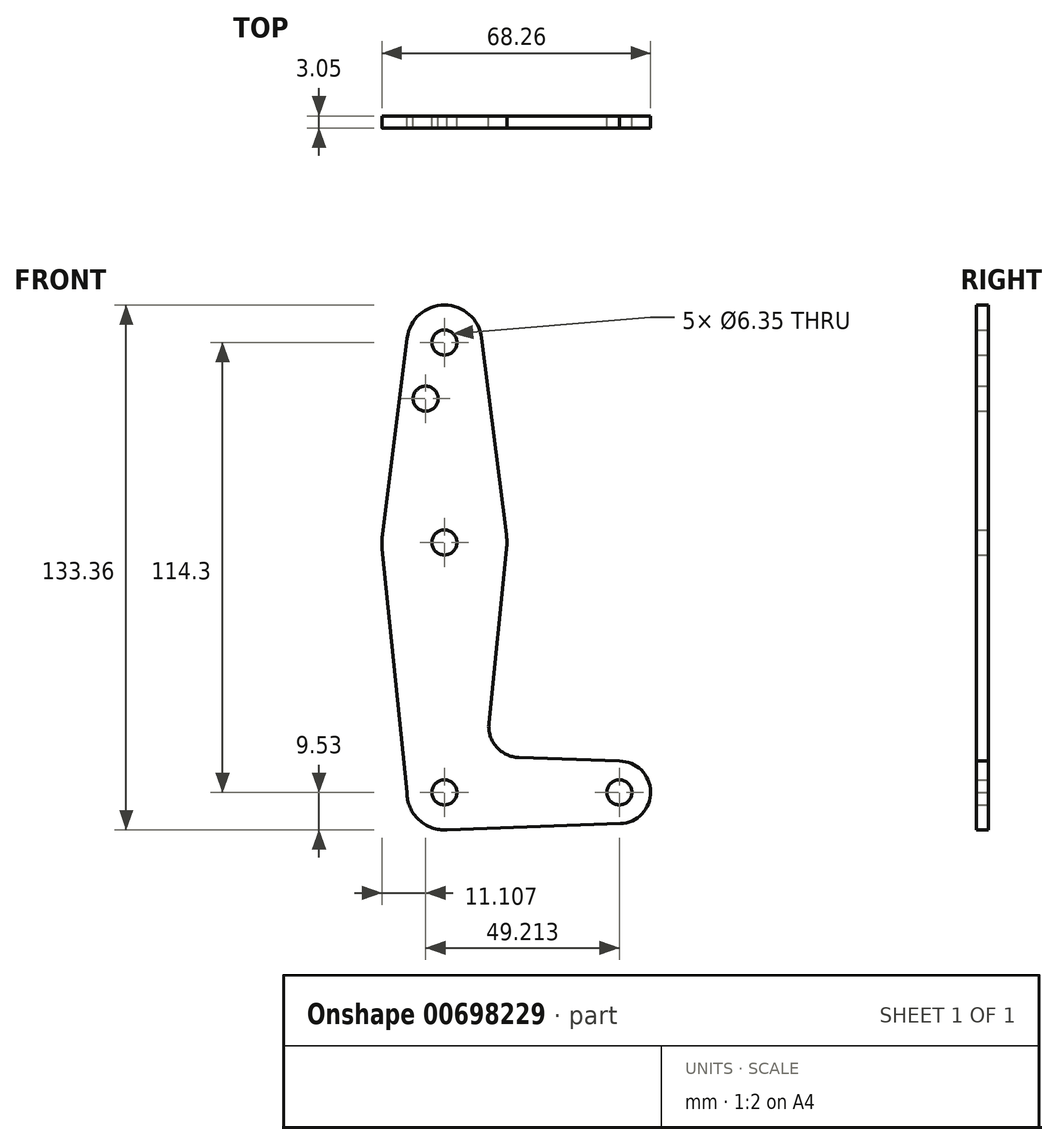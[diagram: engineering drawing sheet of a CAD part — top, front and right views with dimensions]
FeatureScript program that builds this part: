
annotation { "Feature Type Name" : "Feature", "Feature Type Description" : "" }
export const myFeature = defineFeature(function(context is Context, id is Id, definition is map)
    precondition{}
    {
        {
            var Q0;
            Q0=qCreatedBy(makeId("Front.planeOp"),FACE);
            var sketch = newSketch(context, id + "F0", { "sketchPlane" : qUnion([Q0])});
            skLineSegment(sketch, "E0", {"start": v(0, 0) * mm, "end": v(44.45, 0) * mm});
            skLineSegment(sketch, "E1", {"start": v(44.45, 0) * mm, "end": v(0, 0) * mm, "construction": true});
            skLineSegment(sketch, "E2", {"start": v(0, 63.5) * mm, "end": v(0, 114.3) * mm, "construction": true});
            skCircle(sketch, "E3", {"center": v(0, 63.5) * mm, "radius": 15.88 * mm});
            skLineSegment(sketch, "E4", {"start": v(0, 63.5) * mm, "end": v(0, 0) * mm, "construction": true});
            skCircle(sketch, "E5", {"center": v(0, 114.3) * mm, "radius": 9.53 * mm});
            skCircle(sketch, "E6", {"center": v(0, 0) * mm, "radius": 9.53 * mm});
            skCircle(sketch, "E7", {"center": v(44.45, 0) * mm, "radius": 7.94 * mm});
            skLineSegment(sketch, "E8", {"start": v(9.45, 115.5) * mm, "end": v(15.75, 65.48) * mm});
            skLineSegment(sketch, "E9", {"start": v(0, -9.53) * mm, "end": v(44.73, -7.93) * mm});
            skLineSegment(sketch, "E10", {"start": v(44.45, 7.94) * mm, "end": v(18.93, 8.85) * mm});
            skCircle(sketch, "E11", {"center": v(0, 114.3) * mm, "radius": 3.18 * mm});
            skCircle(sketch, "E12", {"center": v(-4.76, 100.03) * mm, "radius": 3.18 * mm});
            skLineSegment(sketch, "E13", {"start": v(15.75, 65.48) * mm, "end": v(9.6, 114.3) * mm});
            skLineSegment(sketch, "E14", {"start": v(-9.45, 115.5) * mm, "end": v(-15.75, 65.48) * mm});
            skCircle(sketch, "E15", {"center": v(0, 63.5) * mm, "radius": 3.18 * mm});
            skCircle(sketch, "E16", {"center": v(0, 0) * mm, "radius": 3.18 * mm});
            skCircle(sketch, "E17", {"center": v(44.45, 0) * mm, "radius": 3.18 * mm});
            skLineSegment(sketch, "E18", {"start": v(-9.52, 0) * mm, "end": v(-15.8, 61.9) * mm});
            skLineSegment(sketch, "E19", {"start": v(11.3, 17.6) * mm, "end": v(15.8, 61.9) * mm});
            skArc(sketch, "E20.filletArc", {"start": v(11.3, 17.6) * mm, "mid": v(13.22, 11.57) * mm, "end": v(18.93, 8.85) * mm});
            skSolve(sketch);
        }
        {
            var Q0;
            Q0 = qSketchRegion(id + "F0", true);
            extrude(context, id + "F1", {"entities" : qUnion([Q0]), "depth" : 3.05 * mm, "offsetDistance" : 25.4 * mm});
        }
    });
